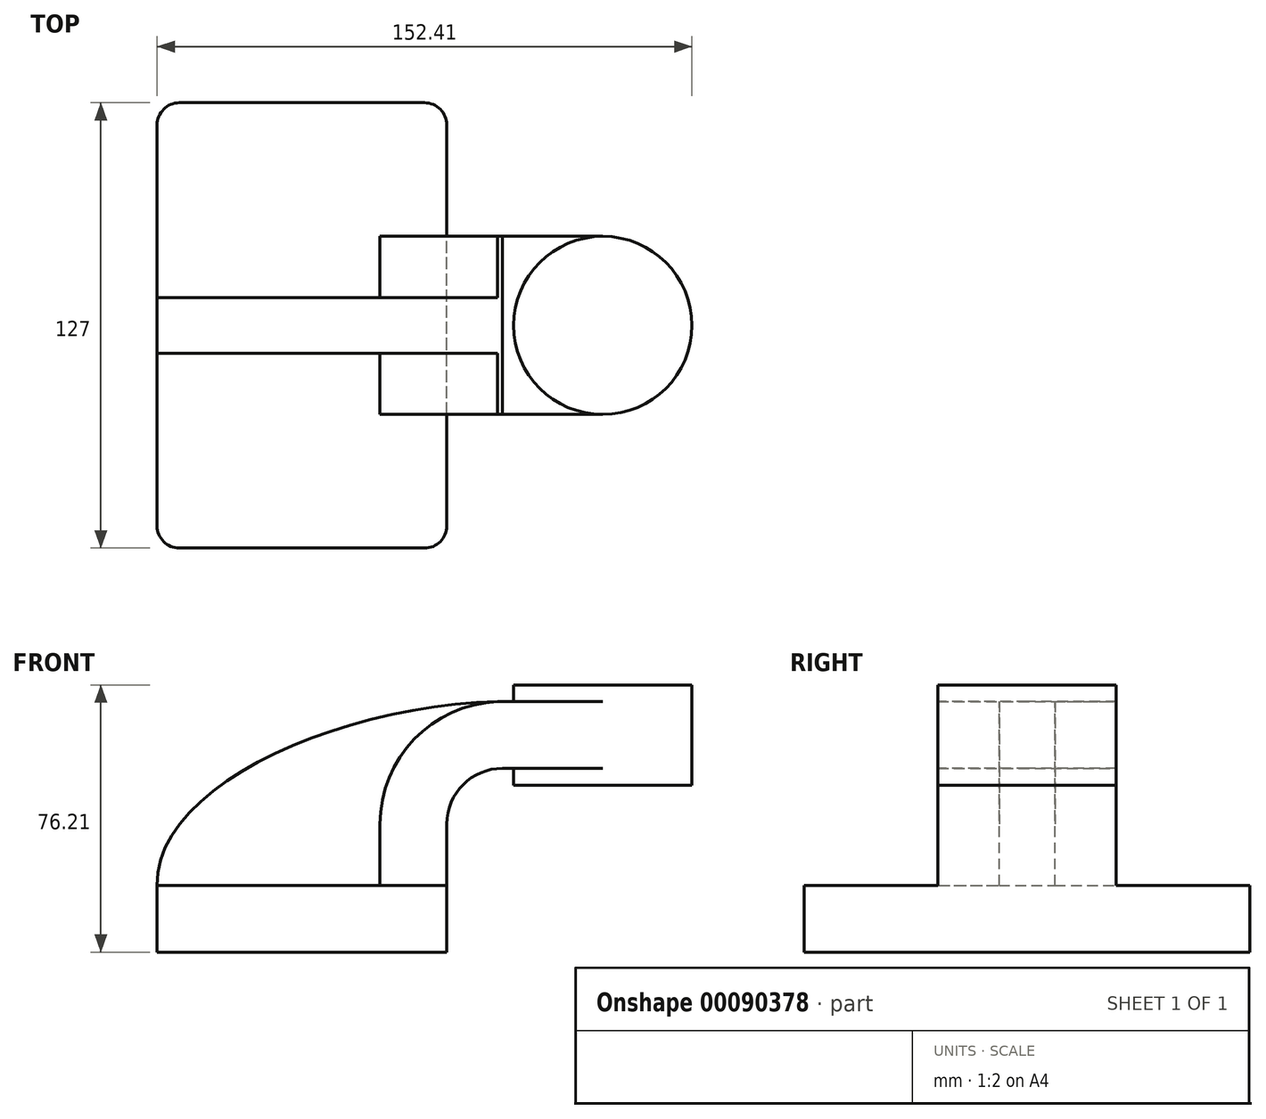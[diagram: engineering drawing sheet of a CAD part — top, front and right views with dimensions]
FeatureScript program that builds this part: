
annotation { "Feature Type Name" : "Feature", "Feature Type Description" : "" }
export const myFeature = defineFeature(function(context is Context, id is Id, definition is map)
    precondition{}
    {
        {
            var Q0;
            Q0=qCreatedBy(makeId("Front.planeOp"),FACE);
            var sketch = newSketch(context, id + "F0", { "sketchPlane" : qUnion([Q0])});
            skLineSegment(sketch, "E0.bottom", {"start": v(-41.28, 9.52) * mm, "end": v(41.27, 9.53) * mm});
            skLineSegment(sketch, "E0.top", {"start": v(-41.28, -9.53) * mm, "end": v(41.28, -9.53) * mm});
            skLineSegment(sketch, "E0.left", {"start": v(-41.28, 9.52) * mm, "end": v(-41.27, -9.53) * mm});
            skLineSegment(sketch, "E0.right", {"start": v(41.28, 9.53) * mm, "end": v(41.28, -9.52) * mm});
            skPoint(sketch, "E0.middle", {"position": v(0, 0) * mm});
            skLineSegment(sketch, "E1.bottom", {"start": v(60.32, 66.67) * mm, "end": v(111.12, 66.67) * mm});
            skLineSegment(sketch, "E1.top", {"start": v(60.32, 38.1) * mm, "end": v(111.12, 38.1) * mm});
            skLineSegment(sketch, "E1.left", {"start": v(60.32, 66.67) * mm, "end": v(60.32, 38.1) * mm});
            skLineSegment(sketch, "E1.right", {"start": v(111.12, 66.68) * mm, "end": v(111.12, 38.1) * mm});
            skPoint(sketch, "E1.middle", {"position": v(85.72, 52.39) * mm});
            skLineSegment(sketch, "E2", {"start": v(41.27, 9.53) * mm, "end": v(41.27, 27) * mm});
            skArc(sketch, "E3", {"start": v(41.27, 27) * mm, "mid": v(45.92, 38.23) * mm, "end": v(57.15, 42.88) * mm});
            skLineSegment(sketch, "E4", {"start": v(57.15, 42.88) * mm, "end": v(85.72, 42.88) * mm});
            skLineSegment(sketch, "E5.0", {"start": v(57.15, 61.93) * mm, "end": v(85.72, 61.93) * mm});
            skArc(sketch, "E5.1", {"start": v(22.23, 27) * mm, "mid": v(32.45, 51.7) * mm, "end": v(57.15, 61.93) * mm});
            skLineSegment(sketch, "E5.2", {"start": v(22.22, 9.53) * mm, "end": v(22.22, 27) * mm});
            skLineSegment(sketch, "E6", {"start": v(85.72, 38.1) * mm, "end": v(85.72, 66.67) * mm});
            skFitSpline(sketch, "E7", {"points": [v(-41.28, 9.52) * mm, v(57.15, 61.93) * mm], "startDerivative": vector(-1.82, 85.4) * mm, "endDerivative": vector(138.86, 2.07) * mm});
            skSolve(sketch);
        }
        {
            var Q0;
            Q0=makeQuery(id+"F0.imprint","IMPRINT",FACE,{"disambiguationData":[TD([[makeQuery(id+"F0.imprint","IMPRINT",EDGE,{"derivedFrom":sQuery(id+"F0.wireOp",EDGE,"E0.top")}),1.0]])]});
            extrude(context, id + "F1", {"entities" : qUnion([Q0]), "endBound" : BoundingType.SYMMETRIC, "depth" : 127 * mm});
        }
        {
            var Q0;
            {var subQ1=sQuery(id+"F0.wireOp",EDGE,"E2");Q0=makeQuery(id+"F0.imprint","IMPRINT",FACE,{"disambiguationData":[TD([[makeQuery(id+"F0.imprint","IMPRINT",EDGE,{"derivedFrom":subQ1}),1.0]])]});}
            var Q1;
            {var subQ0=sQuery(id+"F0.wireOp",EDGE,"E5.0");var subQ1=sQuery(id+"F0.wireOp",EDGE,"E1.left");var subQ2=makeQuery(id+"F0.imprint","INTERSECT",VERTEX,{"derivedFrom":[subQ1,subQ0]});Q1=makeQuery(id+"F0.imprint","IMPRINT",FACE,{"disambiguationData":[TD([[makeQuery(id+"F0.imprint","IMPRINT",EDGE,{"disambiguationData":[TD([[subQ2,-1.0]])],"derivedFrom":subQ1}),1.0]])]});}
            extrude(context, id + "F2", {"entities" : qUnion([Q0, Q1]), "operationType" : NewBodyOperationType.ADD, "endBound" : BoundingType.SYMMETRIC, "depth" : 50.8 * mm});
        }
        {
            var Q0;
            {var subQ3=sQuery(id+"F0.wireOp",EDGE,"E5.2");Q0=makeQuery(id+"F0.imprint","IMPRINT",FACE,{"disambiguationData":[TD([[makeQuery(id+"F0.imprint","IMPRINT",EDGE,{"derivedFrom":subQ3}),1.0]])]});}
            extrude(context, id + "F3", {"entities" : qUnion([Q0]), "operationType" : NewBodyOperationType.ADD, "endBound" : BoundingType.SYMMETRIC, "depth" : 15.88 * mm});
        }
        {
            var Q0;
            {var subQ0=sQuery(id+"F0.wireOp",EDGE,"E1.right");Q0=makeQuery(id+"F0.imprint","IMPRINT",FACE,{"disambiguationData":[TD([[makeQuery(id+"F0.imprint","IMPRINT",EDGE,{"derivedFrom":subQ0}),-1.0]])]});}
            var Q1;
            Q1=sQuery(id+"F0.wireOp",EDGE,"E6");
            revolve(context, id + "F4", {"operationType" : NewBodyOperationType.ADD, "entities" : qUnion([Q0]), "axis" : qUnion([Q1]), "revolveType" : RevolveType.FULL});
        }
        {
            var Q0;
            Q0=makeQuery(id+"F1.opExtrude","CAP_EDGE",EDGE,{"disambiguationData":[OSD([sQuery(id+"F0.wireOp",EDGE,"E0.left")])],"isStart":false});
            var Q1;
            Q1=makeQuery(id+"F1.opExtrude","CAP_EDGE",EDGE,{"disambiguationData":[OSD([sQuery(id+"F0.wireOp",EDGE,"E0.right")])],"isStart":false});
            var Q2;
            Q2=makeQuery(id+"F1.opExtrude","CAP_EDGE",EDGE,{"disambiguationData":[OSD([sQuery(id+"F0.wireOp",EDGE,"E0.left")])],"isStart":true});
            var Q3;
            Q3=makeQuery(id+"F1.opExtrude","CAP_EDGE",EDGE,{"disambiguationData":[OSD([sQuery(id+"F0.wireOp",EDGE,"E0.right")])],"isStart":true});
            fillet(context, id + "F5", {"entities" : qUnion([Q0, Q1, Q2, Q3]), "radius" : 6.35 * mm, "tangentPropagation" : true, "allowEdgeOverflow" : false});
        }
    });
